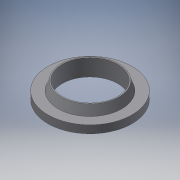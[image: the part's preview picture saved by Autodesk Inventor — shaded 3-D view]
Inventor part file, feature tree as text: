
AUTODESK INVENTOR PART (.ipt)
format: ipt  version: 2017.3 (Build 213257000, 257)  size: 119,808 bytes
history: native  units: in
note: dims shown in document units (in); Inventor stores cm internally (conversion verified against a paired STEP export)
features: revolve x1, sketch x1
ambient origin geometry x8: Origin, YZ Plane, XZ Plane, XY Plane, X Axis, Y Axis, Z Axis, Center Point
bodies: Solid1 (feature_tree)
feature tree (2):
  revolve  "Revolution1"  [1 undecoded]
  sketch  "Sketch1"  dims[d0=13.5in d2=3.75in d3=0.0625in d4=20.375in d5=8.12in d6=15.405in d7=14.0in d8=90.0deg]
note: 1 required parameter value undecoded (feature->parameter linkage not recoverable at this tier; creation-order binding heuristic only, values carry confidence <= 0.55)
